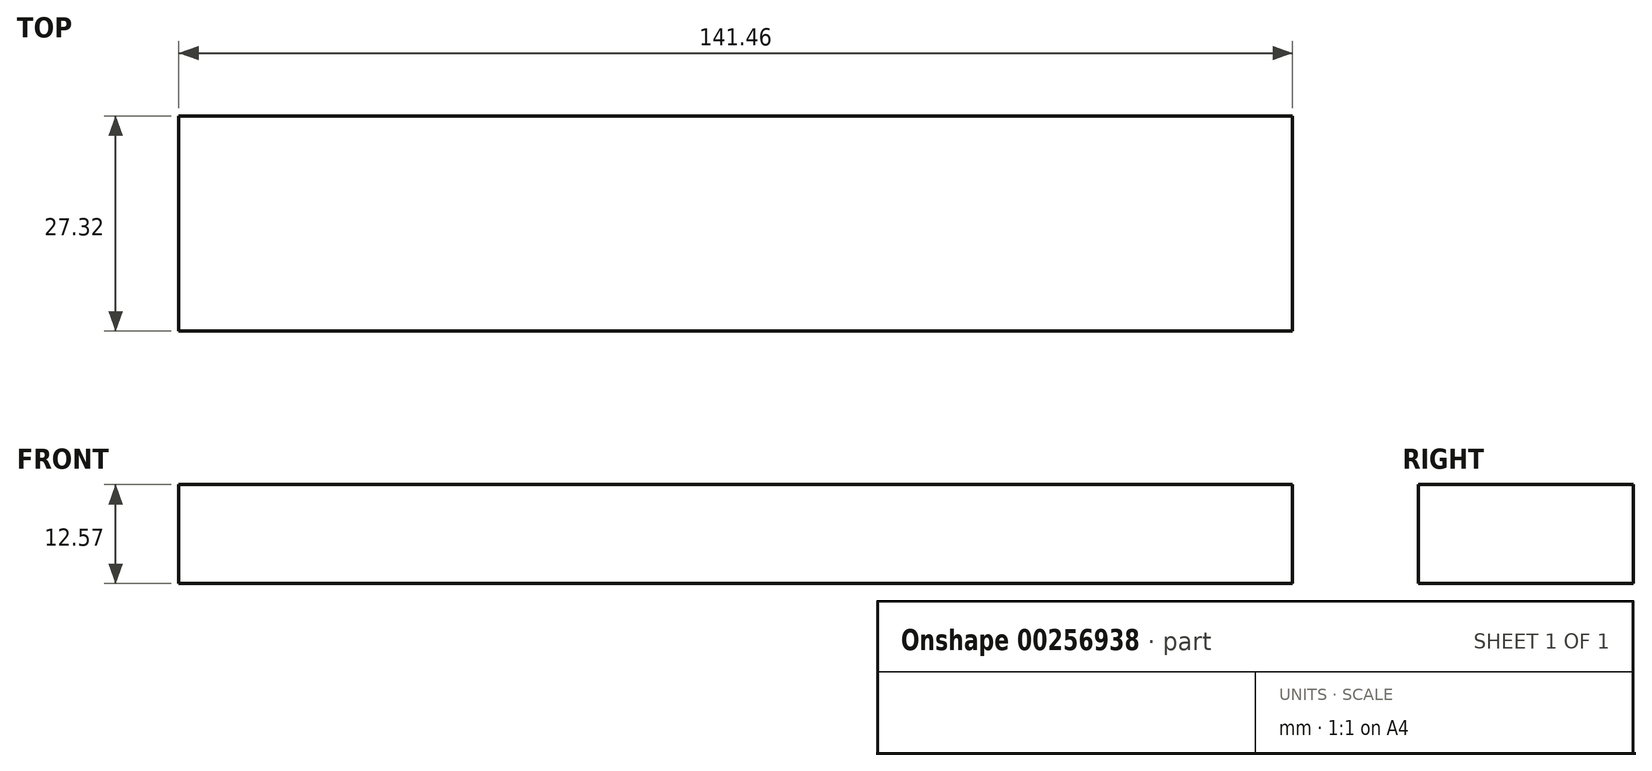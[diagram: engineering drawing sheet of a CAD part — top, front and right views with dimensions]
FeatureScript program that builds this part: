
annotation { "Feature Type Name" : "Feature", "Feature Type Description" : "" }
export const myFeature = defineFeature(function(context is Context, id is Id, definition is map)
    precondition{}
    {
        {
            var Q0;
            Q0=qCreatedBy(makeId("Top.planeOp"),FACE);
            var sketch = newSketch(context, id + "F0", { "sketchPlane" : qUnion([Q0])});
            skLineSegment(sketch, "E0.bottom", {"start": v(-70.73, 13.66) * mm, "end": v(70.73, 13.66) * mm});
            skLineSegment(sketch, "E0.top", {"start": v(-70.73, -13.66) * mm, "end": v(70.73, -13.66) * mm});
            skLineSegment(sketch, "E0.left", {"start": v(-70.73, 13.66) * mm, "end": v(-70.73, -13.66) * mm});
            skLineSegment(sketch, "E0.right", {"start": v(70.73, 13.66) * mm, "end": v(70.73, -13.66) * mm});
            skPoint(sketch, "E0.middle", {"position": v(0, 0) * mm});
            skSolve(sketch);
        }
        {
            var Q0;
            Q0=makeQuery(id+"F0.imprint","IMPRINT",FACE,{"disambiguationData":[TD([[makeQuery(id+"F0.imprint","IMPRINT",EDGE,{"derivedFrom":sQuery(id+"F0.wireOp",EDGE,"E0.bottom")}),-1.0]])]});
            extrude(context, id + "F1", {"entities" : qUnion([Q0]), "depth" : 12.57 * mm});
        }
    });
